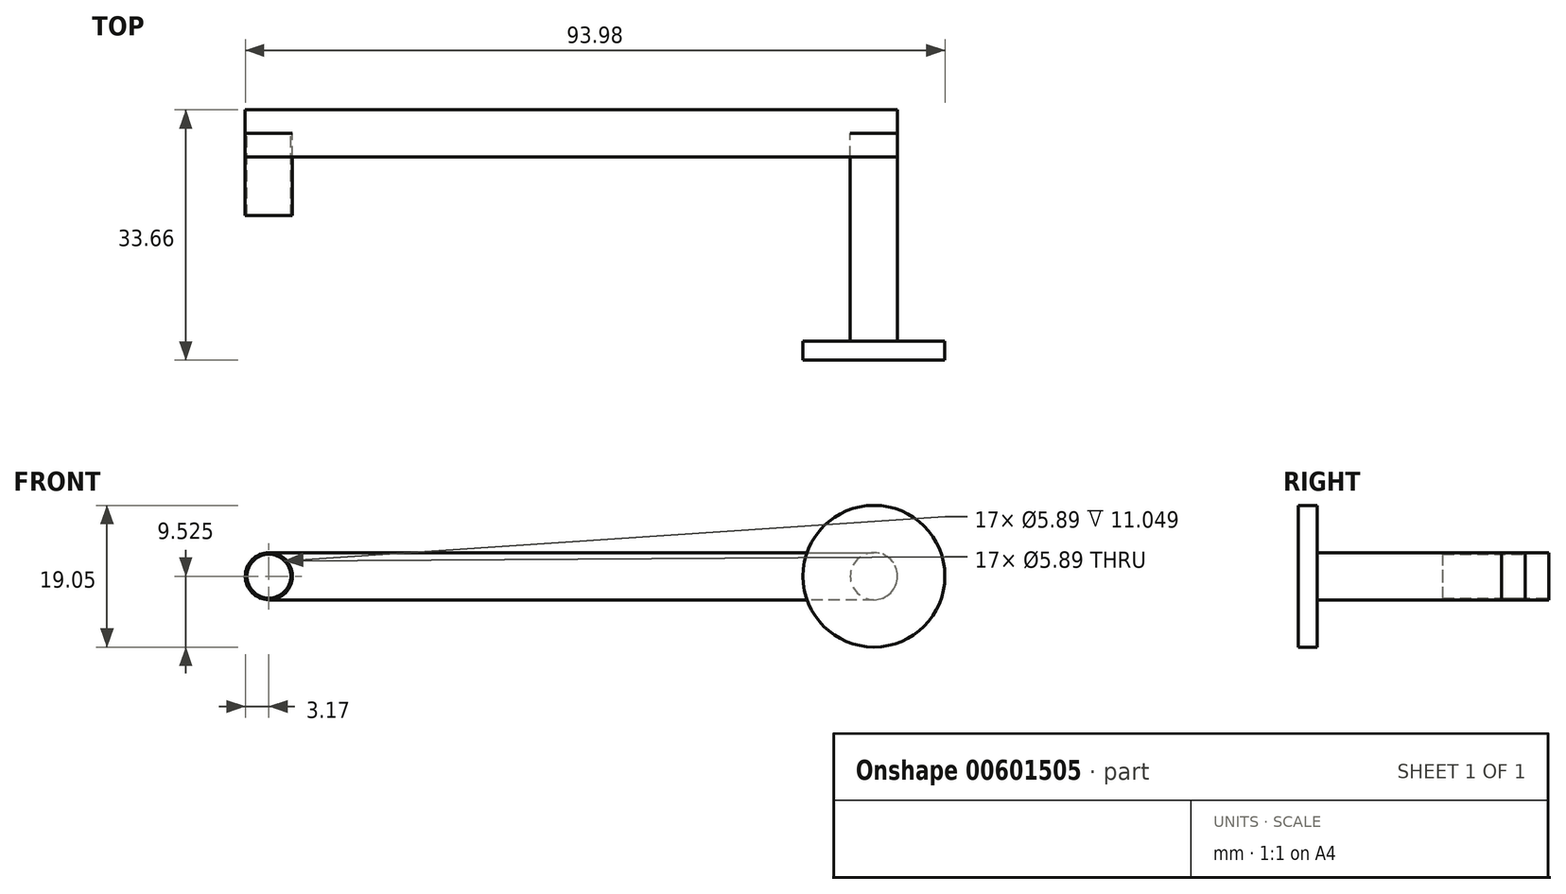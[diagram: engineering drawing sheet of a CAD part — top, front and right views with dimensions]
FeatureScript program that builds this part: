
annotation { "Feature Type Name" : "Feature", "Feature Type Description" : "" }
export const myFeature = defineFeature(function(context is Context, id is Id, definition is map)
    precondition{}
    {
        {
            var Q0;
            Q0=qCreatedBy(makeId("Front.planeOp"),FACE);
            var sketch = newSketch(context, id + "F0", { "sketchPlane" : qUnion([Q0])});
            skLineSegment(sketch, "E0", {"start": v(-35, 6.35) * mm, "end": v(46.28, 6.35) * mm});
            skLineSegment(sketch, "E1", {"start": v(46.28, 6.35) * mm, "end": v(46.28, 0) * mm});
            skLineSegment(sketch, "E2", {"start": v(46.28, 0) * mm, "end": v(-35, 0) * mm});
            skLineSegment(sketch, "E3", {"start": v(-35, 0) * mm, "end": v(-35, 6.35) * mm});
            skArc(sketch, "E4", {"start": v(-35, 6.35) * mm, "mid": v(-38.17, 3.18) * mm, "end": v(-35, 0) * mm});
            skArc(sketch, "E5", {"start": v(46.28, 0) * mm, "mid": v(49.46, 3.17) * mm, "end": v(46.28, 6.35) * mm});
            skCircle(sketch, "E6", {"center": v(-35, 3.18) * mm, "radius": 3.17 * mm});
            skCircle(sketch, "E7", {"center": v(46.28, 3.17) * mm, "radius": 3.18 * mm});
            skLineSegment(sketch, "E8", {"start": v(-35, 3.18) * mm, "end": v(-31.82, 3.18) * mm, "construction": true});
            skLineSegment(sketch, "E9", {"start": v(-31.82, 3.18) * mm, "end": v(-35, 3.18) * mm, "construction": true});
            skLineSegment(sketch, "E10", {"start": v(-35, 3.18) * mm, "end": v(-38.17, 3.18) * mm, "construction": true});
            skCircle(sketch, "E11.0", {"center": v(-35, 3.18) * mm, "radius": 2.95 * mm});
            skSolve(sketch);
        }
        {
            var Q0;
            {var subQ0=sQuery(id+"F0.wireOp",EDGE,"E11.0");var subQ1=sQuery(id+"F0.wireOp",EDGE,"E3");var subQ2=makeQuery(id+"F0.imprint","INTERSECT",VERTEX,{"disambiguationData":[OD(0.0)],"derivedFrom":[subQ1,subQ0]});Q0=makeQuery(id+"F0.imprint","IMPRINT",FACE,{"disambiguationData":[TD([[makeQuery(id+"F0.imprint","IMPRINT",EDGE,{"disambiguationData":[TD([[subQ2,-1.0]])],"derivedFrom":subQ1}),-1.0]])]});}
            var Q1;
            {var subQ0=sQuery(id+"F0.wireOp",EDGE,"E11.0");var subQ1=sQuery(id+"F0.wireOp",EDGE,"E3");var subQ2=makeQuery(id+"F0.imprint","INTERSECT",VERTEX,{"disambiguationData":[OD(0.0)],"derivedFrom":[subQ1,subQ0]});Q1=makeQuery(id+"F0.imprint","IMPRINT",FACE,{"disambiguationData":[TD([[makeQuery(id+"F0.imprint","IMPRINT",EDGE,{"disambiguationData":[TD([[subQ2,-1.0]])],"derivedFrom":subQ1}),1.0]])]});}
            extrude(context, id + "F1", {"entities" : qUnion([Q0, Q1]), "depth" : 11.05 * mm, "offsetDistance" : 25.4 * mm});
        }
        {
            var Q0;
            {var subQ0=sQuery(id+"F0.wireOp",EDGE,"E1");Q0=makeQuery(id+"F0.imprint","IMPRINT",FACE,{"disambiguationData":[TD([[makeQuery(id+"F0.imprint","IMPRINT",EDGE,{"derivedFrom":subQ0}),-1.0]])]});}
            var Q1;
            {var subQ0=sQuery(id+"F0.wireOp",EDGE,"E1");Q1=makeQuery(id+"F0.imprint","IMPRINT",FACE,{"disambiguationData":[TD([[makeQuery(id+"F0.imprint","IMPRINT",EDGE,{"derivedFrom":subQ0}),1.0]])]});}
            extrude(context, id + "F2", {"entities" : qUnion([Q0, Q1]), "depth" : 27.94 * mm, "offsetDistance" : 25.4 * mm});
        }
        {
            var Q0;
            {var subQ0=sQuery(id+"F0.wireOp",EDGE,"E0");Q0=makeQuery(id+"F0.imprint","IMPRINT",FACE,{"disambiguationData":[TD([[makeQuery(id+"F0.imprint","IMPRINT",EDGE,{"derivedFrom":subQ0}),-1.0]])]});}
            var Q1;
            {var subQ1=sQuery(id+"F0.wireOp",EDGE,"E3");var subQ3=sQuery(id+"F0.wireOp",EDGE,"E11.0");var subQ4=makeQuery(id+"F0.imprint","INTERSECT",VERTEX,{"disambiguationData":[OD(0.0)],"derivedFrom":[subQ1,subQ3]});Q1=makeQuery(id+"F0.imprint","IMPRINT",FACE,{"disambiguationData":[TD([[makeQuery(id+"F0.imprint","IMPRINT",EDGE,{"disambiguationData":[TD([[subQ4,1.0]])],"derivedFrom":subQ3}),-1.0]])]});}
            var Q2;
            {var subQ1=sQuery(id+"F0.wireOp",EDGE,"E3");var subQ3=sQuery(id+"F0.wireOp",EDGE,"E11.0");var subQ4=makeQuery(id+"F0.imprint","INTERSECT",VERTEX,{"disambiguationData":[OD(0.0)],"derivedFrom":[subQ1,subQ3]});Q2=makeQuery(id+"F0.imprint","IMPRINT",FACE,{"disambiguationData":[TD([[makeQuery(id+"F0.imprint","IMPRINT",EDGE,{"disambiguationData":[TD([[subQ4,-1.0]])],"derivedFrom":subQ3}),-1.0]])]});}
            var Q3;
            {var subQ0=sQuery(id+"F0.wireOp",EDGE,"E1");Q3=makeQuery(id+"F0.imprint","IMPRINT",FACE,{"disambiguationData":[TD([[makeQuery(id+"F0.imprint","IMPRINT",EDGE,{"derivedFrom":subQ0}),1.0]])]});}
            var Q4;
            {var subQ0=sQuery(id+"F0.wireOp",EDGE,"E1");Q4=makeQuery(id+"F0.imprint","IMPRINT",FACE,{"disambiguationData":[TD([[makeQuery(id+"F0.imprint","IMPRINT",EDGE,{"derivedFrom":subQ0}),-1.0]])]});}
            var Q5;
            {var subQ0=sQuery(id+"F0.wireOp",EDGE,"E11.0");var subQ1=sQuery(id+"F0.wireOp",EDGE,"E3");var subQ2=makeQuery(id+"F0.imprint","INTERSECT",VERTEX,{"disambiguationData":[OD(0.0)],"derivedFrom":[subQ1,subQ0]});Q5=makeQuery(id+"F0.imprint","IMPRINT",FACE,{"disambiguationData":[TD([[makeQuery(id+"F0.imprint","IMPRINT",EDGE,{"disambiguationData":[TD([[subQ2,-1.0]])],"derivedFrom":subQ1}),1.0]])]});}
            var Q6;
            {var subQ0=sQuery(id+"F0.wireOp",EDGE,"E11.0");var subQ1=sQuery(id+"F0.wireOp",EDGE,"E3");var subQ2=makeQuery(id+"F0.imprint","INTERSECT",VERTEX,{"disambiguationData":[OD(0.0)],"derivedFrom":[subQ1,subQ0]});Q6=makeQuery(id+"F0.imprint","IMPRINT",FACE,{"disambiguationData":[TD([[makeQuery(id+"F0.imprint","IMPRINT",EDGE,{"disambiguationData":[TD([[subQ2,-1.0]])],"derivedFrom":subQ1}),-1.0]])]});}
            extrude(context, id + "F3", {"entities" : qUnion([Q0, Q1, Q2, Q3, Q4, Q5, Q6]), "depth" : 6.35 * mm, "offsetDistance" : 25.4 * mm, "symmetric" : true});
        }
        {
            var Q0;
            Q0=makeQuery(id+"F2.opExtrude","CAP_FACE",FACE,{"disambiguationData":[OSD([sQuery(id+"F0.wireOp",EDGE,"E7")])],"isStart":false});
            var sketch = newSketch(context, id + "F4", { "sketchPlane" : qUnion([Q0])});
            skLineSegment(sketch, "E12", {"start": v(46.28, 3.17) * mm, "end": v(46.28, 6.35) * mm});
            skCircle(sketch, "E13", {"center": v(46.28, 3.17) * mm, "radius": 3.18 * mm});
            skCircle(sketch, "E14.0", {"center": v(46.28, 3.17) * mm, "radius": 9.52 * mm});
            skSolve(sketch);
        }
        {
            var Q0;
            Q0=makeQuery(id+"F4.imprint","IMPRINT",FACE,{"disambiguationData":[TD([[makeQuery(id+"F4.imprint","IMPRINT",EDGE,{"derivedFrom":sQuery(id+"F4.wireOp",EDGE,"E13")}),1.0]])]});
            var Q1;
            Q1=makeQuery(id+"F4.imprint","IMPRINT",FACE,{"disambiguationData":[TD([[makeQuery(id+"F4.imprint","IMPRINT",EDGE,{"derivedFrom":sQuery(id+"F4.wireOp",EDGE,"E13")}),-1.0]])]});
            extrude(context, id + "F5", {"entities" : qUnion([Q0, Q1]), "operationType" : NewBodyOperationType.ADD, "depth" : 2.54 * mm, "offsetDistance" : 25.4 * mm});
        }
    });
